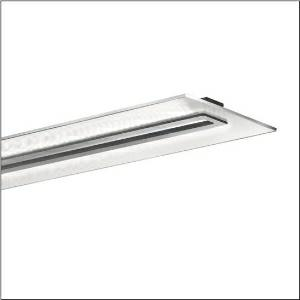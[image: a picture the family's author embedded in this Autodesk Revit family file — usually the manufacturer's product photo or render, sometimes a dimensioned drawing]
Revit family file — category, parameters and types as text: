
# Revit family: vega_r__11_5mn238dlc0s_c747
name_source: partatom
category: Lighting Fixtures
units: mm (PartAtom-declared; Revit-internal decimal feet)

## family parameters
Cut with Voids When Loaded = No
Host = Face
Light Source = No
Part Type = Normal
Room Calculation Point = No
Round Connector Dimension = Use Diameter
Shared = No

## types (1)
- --- (1 x LED 4000K / CRI = 80, 4300 lm, 31 W, 4000K)
    Apparent Load = 31 VA
    Color Rendering = 83
    Color Temperature = 4000K
    Default Elevation = 1800 mm
    Description = Vega® 11, office luminaire, primary light control with prismatic reflector, of PMMA, transparent prismatic structure, CAT 2 (L<= 1500cd/m²), light emission: direct/indirect distribution, primary light characteristic: symmetric, installation type: suspended mounting, surface-mounted, LED rated luminous flux: 4.300 lm, light colour: 840, colour temperature: 4000K, control gear: ECG, with terminal, 3+2-pole, max. 2.5mm², mains connection: 230V, AC, 50Hz, connection cable inclusive, cable length: 1,5 m, rated input power: 31W, luminaire housing, rectangular, rounded, of aluminium section, anodised, metallic grey (RAL 9006), length: 1.250 mm, width: 350 mm, height: 43mm, luminaire housing, lower part, of aluminium section, anodised, metallic grey (RAL 9006), of PC, grey, protection rating (complete): IP20, insulation class (complete): insulation class I (protective earthing), certification: CE, permissible ambient temperature for indoor applications: 0..+35°C, standard: EN 50419, packaging unit: 1 piece
    Height = 40 mm  [stored 0.131234 ft]
    Lamp = 1 x LED 4000K / CRI >= 80
    Lamp Light Flux = 4300 lm
    Lamp Power = 31 W
    Lamp count = 1
    Length = 1250 mm
    Luminous efficacy = 0 lm/W
    Manufacturer = Siteco
    ModVariant = No
    Model = 5MN238DLC0S
    Mounting Place = Ceiling
    Mounting Type = Pendant
    Number of Poles = 1
    OnlyDefault = Yes
    Power Factor = 1
    Product Name = Vega® 11
    Product group = office luminaire | ceiling pendant
    ProductGroupID = 905
    Protection Class = Protection class I
    Protection Degree = IP 20
    RLX_Detail_Level = 1
    RlxData = <blob elided: 60377 chars, md5=1f9b08ad>
    Socket = socket
    Standby Power = 0 W
    System Light Flux = 0 lm
    System Power = 31 W
    Type Comments = factory setting: luminous flux: 100 % | dim-lin: 254 | 231 mA
    Type Image = l_1004807.jpg
    URL = http://relux.com
    VarID = @adj_147329
    Voltage = 0 V
    Weight = 0.00 kg
    Width = 350 mm

note: [stored X ft] marks values corroborated as IEEE doubles in the binary element streams (Revit-internal decimal feet)

## geometry (parser evidence)
native form markers: Blend x4, Sweep x11
no freeform markers — native parametric forms only
